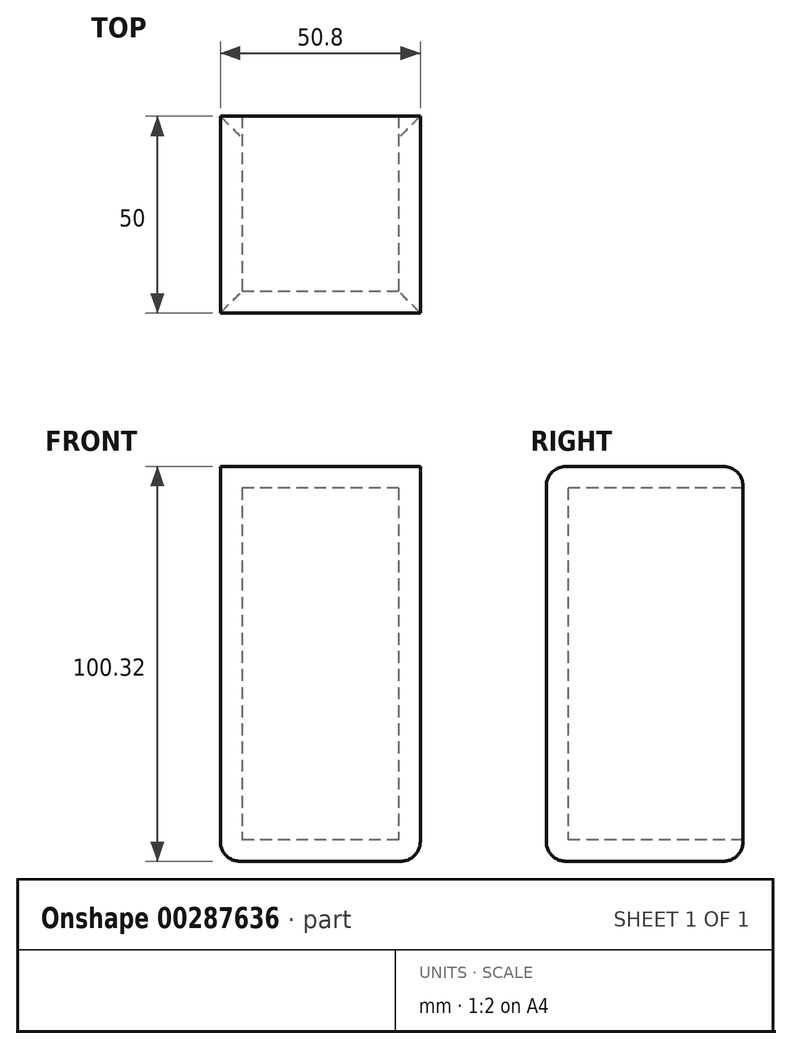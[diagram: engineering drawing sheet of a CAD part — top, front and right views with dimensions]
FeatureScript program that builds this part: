
annotation { "Feature Type Name" : "Feature", "Feature Type Description" : "" }
export const myFeature = defineFeature(function(context is Context, id is Id, definition is map)
    precondition{}
    {
        {
            var Q0;
            Q0=qCreatedBy(makeId("Front.planeOp"),FACE);
            var sketch = newSketch(context, id + "F0", { "sketchPlane" : qUnion([Q0])});
            skLineSegment(sketch, "E0.bottom", {"start": v(-50.8, 0) * mm, "end": v(0, 0) * mm});
            skLineSegment(sketch, "E0.top", {"start": v(-50.8, -100.32) * mm, "end": v(0, -100.32) * mm});
            skLineSegment(sketch, "E0.left", {"start": v(-50.8, 0) * mm, "end": v(-50.8, -100.32) * mm});
            skLineSegment(sketch, "E0.right", {"start": v(0, 0) * mm, "end": v(0, -100.32) * mm});
            skSolve(sketch);
        }
        {
            var Q0;
            Q0=makeQuery(id+"F0.imprint","IMPRINT",FACE,{"disambiguationData":[TD([[makeQuery(id+"F0.imprint","IMPRINT",EDGE,{"derivedFrom":sQuery(id+"F0.wireOp",EDGE,"E0.bottom")}),-1.0]])]});
            extrude(context, id + "F1", {"entities" : qUnion([Q0]), "oppositeDirection" : true, "depth" : 50 * mm});
        }
        {
            var Q0;
            Q0=makeQuery(id+"F1.opExtrude","CAP_EDGE",EDGE,{"disambiguationData":[OSD([sQuery(id+"F0.wireOp",EDGE,"E0.top")])],"isStart":false});
            var Q1;
            Q1=makeQuery(id+"F1.opExtrude","CAP_EDGE",EDGE,{"disambiguationData":[OSD([sQuery(id+"F0.wireOp",EDGE,"E0.bottom")])],"isStart":false});
            var Q2;
            Q2=makeQuery(id+"F1.opExtrude","CAP_EDGE",EDGE,{"disambiguationData":[OSD([sQuery(id+"F0.wireOp",EDGE,"E0.bottom")])],"isStart":true});
            var Q3;
            Q3=makeQuery(id+"F1.opExtrude","CAP_EDGE",EDGE,{"disambiguationData":[OSD([sQuery(id+"F0.wireOp",EDGE,"E0.top")])],"isStart":true});
            var Q4;
            Q4=makeQuery(id+"F1.opExtrude","SWEPT_EDGE",EDGE,{"disambiguationData":[OSD([sQuery(id+"F0.wireOp",EDGE,"E0.top"),sQuery(id+"F0.wireOp",EDGE,"E0.left")])]});
            var Q5;
            Q5=makeQuery(id+"F1.opExtrude","SWEPT_EDGE",EDGE,{"disambiguationData":[OSD([sQuery(id+"F0.wireOp",EDGE,"E0.top"),sQuery(id+"F0.wireOp",EDGE,"E0.right")])]});
            fillet(context, id + "F2", {"entities" : qUnion([Q0, Q1, Q2, Q3, Q4, Q5]), "radius" : 5 * mm, "tangentPropagation" : true, "allowEdgeOverflow" : false});
        }
        {
            var Q0;
            Q0=makeQuery(id+"F1.opExtrude","CAP_FACE",FACE,{"disambiguationData":[OSD([sQuery(id+"F0.wireOp",EDGE,"E0.bottom"),sQuery(id+"F0.wireOp",EDGE,"E0.top"),sQuery(id+"F0.wireOp",EDGE,"E0.left"),sQuery(id+"F0.wireOp",EDGE,"E0.right")])],"isStart":false});
            shell(context, id + "F3", {"entities" : qUnion([Q0]), "thickness" : 5.5 * mm});
        }
    });
